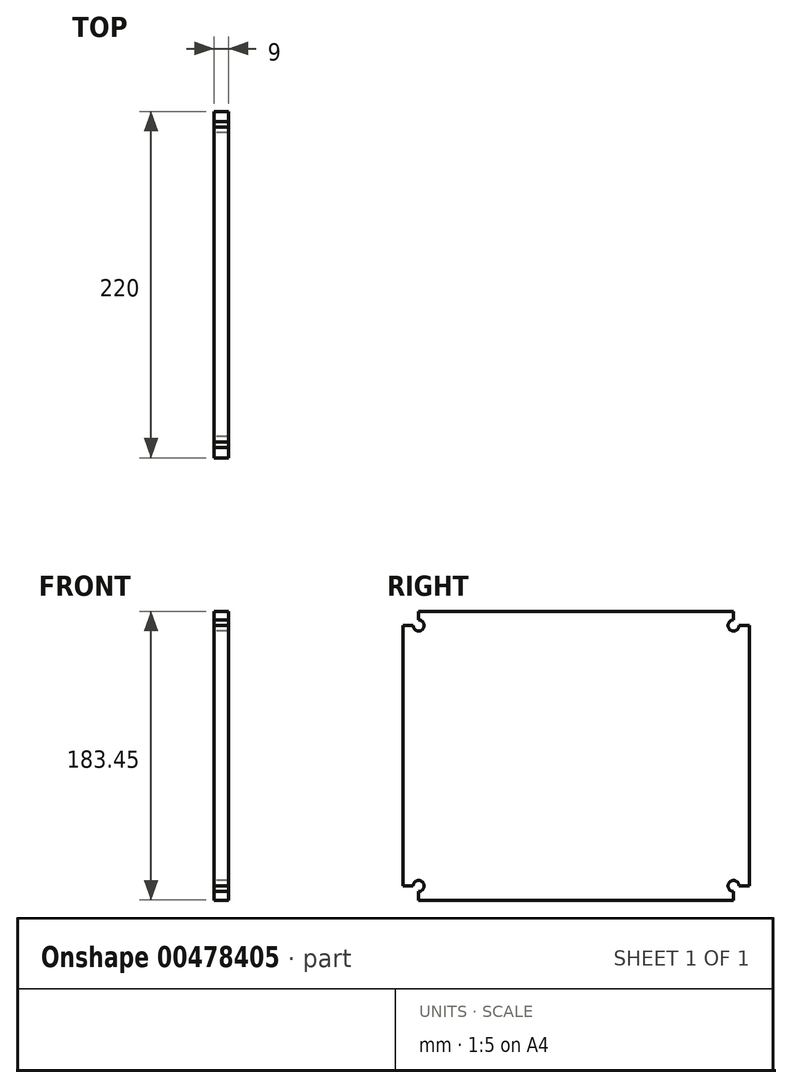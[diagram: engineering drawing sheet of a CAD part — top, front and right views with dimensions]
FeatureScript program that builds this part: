
annotation { "Feature Type Name" : "Feature", "Feature Type Description" : "" }
export const myFeature = defineFeature(function(context is Context, id is Id, definition is map)
    precondition{}
    {
        {
            var Q0;
            Q0=qCreatedBy(makeId("Right.planeOp"),FACE);
            var sketch = newSketch(context, id + "F0", { "sketchPlane" : qUnion([Q0])});
            skLineSegment(sketch, "E0.bottom", {"start": v(-78.05, 116.62) * mm, "end": v(-71.55, 116.62) * mm});
            skLineSegment(sketch, "E0.top", {"start": v(-78.05, -48.83) * mm, "end": v(-71.55, -48.83) * mm});
            skLineSegment(sketch, "E1.0", {"start": v(31.95, 67.29) * mm, "end": v(31.95, -98.17) * mm, "construction": true});
            skLineSegment(sketch, "E2.0", {"start": v(-68.05, 125.62) * mm, "end": v(31.95, 125.62) * mm});
            skLineSegment(sketch, "E3", {"start": v(-68.05, 125.62) * mm, "end": v(-68.05, 120.12) * mm});
            skArc(sketch, "E4", {"start": v(-68.05, 120.12) * mm, "mid": v(-65.57, 114.15) * mm, "end": v(-71.55, 116.62) * mm});
            skLineSegment(sketch, "E5", {"start": v(31.95, -57.83) * mm, "end": v(-68.05, -57.83) * mm});
            skLineSegment(sketch, "E6", {"start": v(-68.05, -57.83) * mm, "end": v(-68.05, -52.33) * mm});
            skArc(sketch, "E7", {"start": v(-71.55, -48.83) * mm, "mid": v(-65.57, -46.36) * mm, "end": v(-68.05, -52.33) * mm});
            skLineSegment(sketch, "E8", {"start": v(-78.05, 116.62) * mm, "end": v(-78.05, -48.83) * mm});
            skLineSegment(sketch, "E9.MirrorCS", {"start": v(141.95, -48.83) * mm, "end": v(135.45, -48.83) * mm});
            skLineSegment(sketch, "E10.MirrorCS", {"start": v(131.95, 125.62) * mm, "end": v(131.95, 120.12) * mm});
            skLineSegment(sketch, "E11.MirrorCS", {"start": v(141.95, 116.62) * mm, "end": v(135.45, 116.62) * mm});
            skLineSegment(sketch, "E12.MirrorCS", {"start": v(131.95, -57.83) * mm, "end": v(131.95, -52.33) * mm});
            skLineSegment(sketch, "E13.MirrorCS", {"start": v(141.95, 116.62) * mm, "end": v(141.95, -48.83) * mm});
            skArc(sketch, "E14.MirrorCS", {"start": v(131.95, 120.12) * mm, "mid": v(129.48, 114.15) * mm, "end": v(135.45, 116.62) * mm});
            skArc(sketch, "E15.MirrorCS", {"start": v(135.45, -48.83) * mm, "mid": v(129.48, -46.36) * mm, "end": v(131.95, -52.33) * mm});
            skLineSegment(sketch, "E16.MirrorCS", {"start": v(31.95, -57.83) * mm, "end": v(131.95, -57.83) * mm});
            skLineSegment(sketch, "E17.MirrorCS", {"start": v(131.95, 125.62) * mm, "end": v(31.95, 125.62) * mm});
            skSolve(sketch);
        }
        {
            var Q0;
            Q0=makeQuery(id+"F0.imprint","IMPRINT",FACE,{"disambiguationData":[TD([[makeQuery(id+"F0.imprint","IMPRINT",EDGE,{"derivedFrom":sQuery(id+"F0.wireOp",EDGE,"E0.bottom")}),-1.0]])]});
            extrude(context, id + "F1", {"entities" : qUnion([Q0]), "depth" : 9 * mm});
        }
    });
